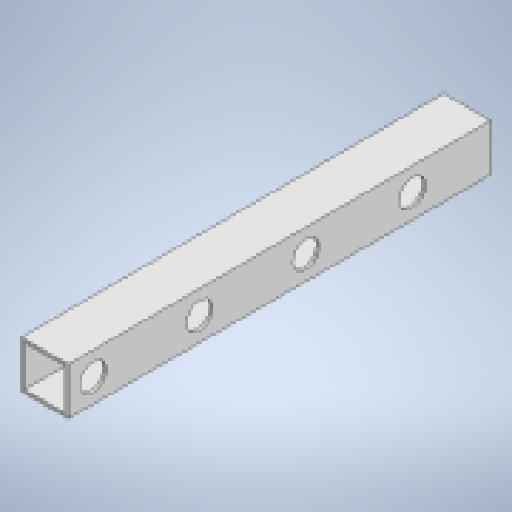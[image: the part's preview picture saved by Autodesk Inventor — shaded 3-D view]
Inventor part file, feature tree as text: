
AUTODESK INVENTOR PART (.ipt)
format: ipt  version: 2025.4 (Build 294407000, 407)  size: 188,416 bytes
history: native  units: mm
features: extrude x2, sketch x2, pattern_linear x1
ambient origin geometry x8: Origin, YZ Plane, XZ Plane, XY Plane, X Axis, Y Axis, Z Axis, Center Point
bodies: Body1 (feature_tree)
feature tree (5):
  extrude  "Extrusion3"  Depth=30.0mm
  extrude  "Extrusion4"  Depth=2.0mm
  pattern_linear  "Rectangular Pattern4"  Count1=27 Spacing1=0.0mm
  sketch  "Sketch9"  dims[d61=320.0mm d172=30.0mm]
  sketch  "Sketch10"  dims[d173=30.0mm d174=2.0mm d175=270.0mm d176=0.0mm d177=17.0mm d178=17.0mm d179=0.0mm d180=0.0mm d181=30.0mm d182=80.0mm d186=17.0mm d187=40.0mm d189=68.0mm]
